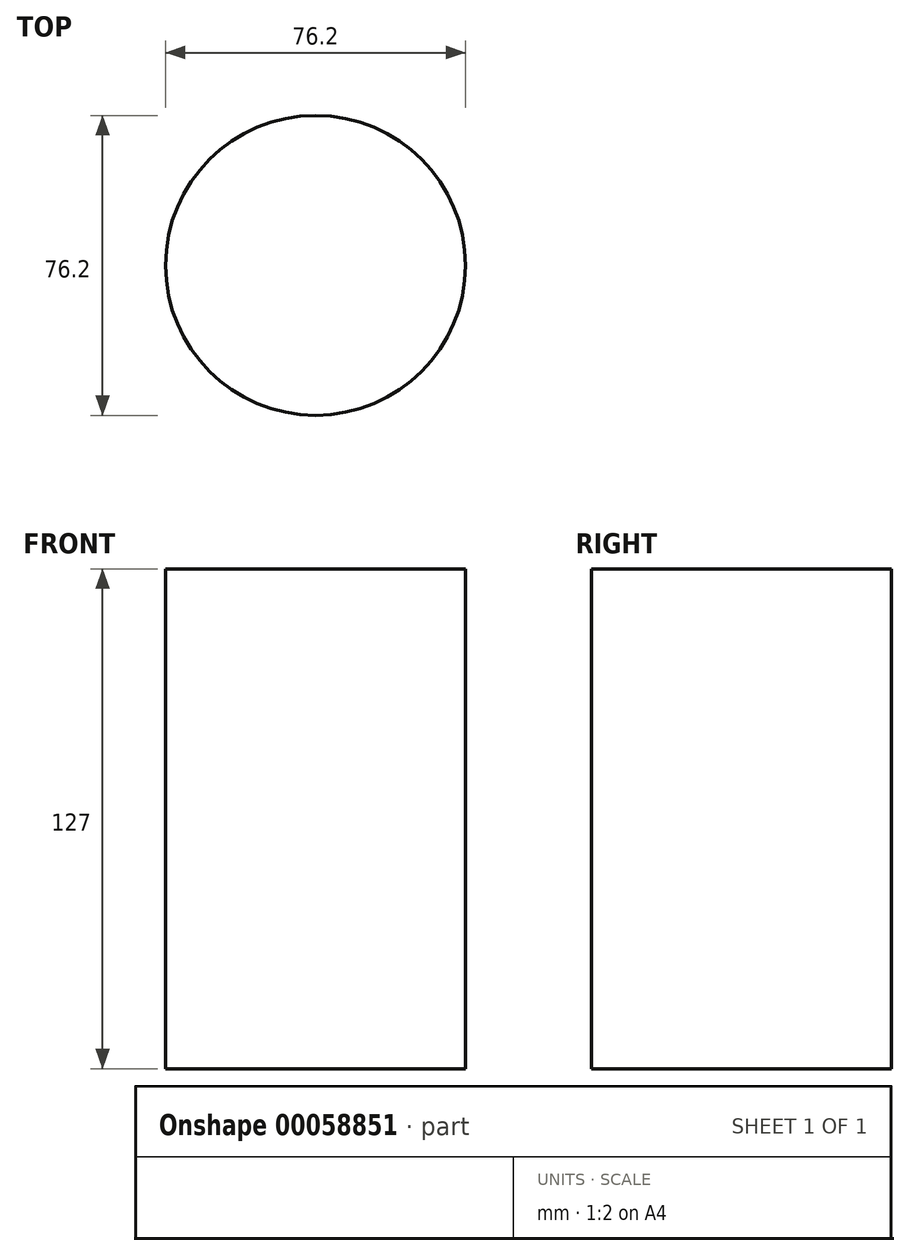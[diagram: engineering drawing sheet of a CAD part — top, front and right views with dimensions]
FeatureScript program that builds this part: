
annotation { "Feature Type Name" : "Feature", "Feature Type Description" : "" }
export const myFeature = defineFeature(function(context is Context, id is Id, definition is map)
    precondition{}
    {
        {
            var Q0;
            Q0=qCreatedBy(makeId("Front.planeOp"),FACE);
            var sketch = newSketch(context, id + "F0", { "sketchPlane" : qUnion([Q0])});
            skLineSegment(sketch, "E0.bottom", {"start": v(-38.1, 63.5) * mm, "end": v(0, 63.5) * mm});
            skLineSegment(sketch, "E0.top", {"start": v(-38.1, -63.5) * mm, "end": v(0, -63.5) * mm});
            skLineSegment(sketch, "E0.left", {"start": v(-38.1, 63.5) * mm, "end": v(-38.1, -63.5) * mm});
            skLineSegment(sketch, "E0.right", {"start": v(0, 63.5) * mm, "end": v(0, -63.5) * mm});
            skSolve(sketch);
        }
        {
            var Q0;
            Q0=makeQuery(id+"F0.imprint","IMPRINT",FACE,{"disambiguationData":[TD([[makeQuery(id+"F0.imprint","IMPRINT",EDGE,{"derivedFrom":sQuery(id+"F0.wireOp",EDGE,"E0.bottom")}),-1.0]])]});
            var Q1;
            Q1=sQuery(id+"F0.wireOp",EDGE,"E0.right");
            revolve(context, id + "F1", {"entities" : qUnion([Q0]), "axis" : qUnion([Q1]), "revolveType" : RevolveType.FULL});
        }
        {
            var Q0;
            Q0=qCreatedBy(makeId("Front.planeOp"),FACE);
            var Q1;
            Q1 = qBodyType(qCreatedBy(id + "F3" ,EDGE), BodyType.WIRE);
            cPlane(context, id + "F2", {"entities" : qUnion([Q0, Q1]), "cplaneType" : CPlaneType.OFFSET, "offset" : 38.1 * mm, "width" : 152.4 * mm, "height" : 152.4 * mm});
        }
        {
            var Q0;
            Q0=qCreatedBy(id+"F2.planeOp",FACE);
            var sketch = newSketch(context, id + "F3", { "sketchPlane" : qUnion([Q0])});
            skCircle(sketch, "E1", {"center": v(0, 0) * mm, "radius": 6.35 * mm});
            skSolve(sketch);
        }
        {
            var Q0;
            Q0=makeQuery(id+"F3.imprint","IMPRINT",FACE,{"disambiguationData":[TD([[makeQuery(id+"F3.imprint","IMPRINT",EDGE,{"derivedFrom":sQuery(id+"F3.wireOp",EDGE,"E1")}),1.0]])]});
            extrude(context, id + "F4", {"entities" : qUnion([Q0]), "depth" : 12.7 * mm});
        }
        {
            var Q0;
            Q0=makeQuery(id+"F4.opExtrude","SWEPT_BODY",BODY,{"disambiguationData":[OSD([sQuery(id+"F3.wireOp",EDGE,"E1")])]});
            var Q1;
            Q1=makeQuery(id+"F1.opRevolve","SWEPT_EDGE",EDGE,{"disambiguationData":[OSD([sQuery(id+"F0.wireOp",EDGE,"E0.bottom"),sQuery(id+"F0.wireOp",EDGE,"E0.left")])]});
            circularPattern(context, id + "F5", {"entities" : qUnion([Q0]), "axis" : qUnion([Q1]), "angle" : 360 * degree, "instanceCount" : round(8), "equalSpace" : true});
        }
        {
            var Q0;
            Q0=makeQuery(id+"F4.opExtrude","SWEPT_BODY",BODY,{"disambiguationData":[OSD([sQuery(id+"F3.wireOp",EDGE,"E1")])]});
            var Q1;
            Q1=makeQuery(id+"F5.opPattern","COPY",BODY,{"derivedFrom":makeQuery(id+"F4.opExtrude","SWEPT_BODY",BODY,{"disambiguationData":[OSD([sQuery(id+"F3.wireOp",EDGE,"E1")])]}),"instanceName":"1"});
            var Q2;
            Q2=makeQuery(id+"F5.opPattern","COPY",BODY,{"derivedFrom":makeQuery(id+"F4.opExtrude","SWEPT_BODY",BODY,{"disambiguationData":[OSD([sQuery(id+"F3.wireOp",EDGE,"E1")])]}),"instanceName":"2"});
            var Q3;
            Q3=makeQuery(id+"F5.opPattern","COPY",BODY,{"derivedFrom":makeQuery(id+"F4.opExtrude","SWEPT_BODY",BODY,{"disambiguationData":[OSD([sQuery(id+"F3.wireOp",EDGE,"E1")])]}),"instanceName":"3"});
            var Q4;
            Q4=makeQuery(id+"F5.opPattern","COPY",BODY,{"derivedFrom":makeQuery(id+"F4.opExtrude","SWEPT_BODY",BODY,{"disambiguationData":[OSD([sQuery(id+"F3.wireOp",EDGE,"E1")])]}),"instanceName":"4"});
            var Q5;
            Q5=makeQuery(id+"F5.opPattern","COPY",BODY,{"derivedFrom":makeQuery(id+"F4.opExtrude","SWEPT_BODY",BODY,{"disambiguationData":[OSD([sQuery(id+"F3.wireOp",EDGE,"E1")])]}),"instanceName":"5"});
            var Q6;
            Q6=makeQuery(id+"F5.opPattern","COPY",BODY,{"derivedFrom":makeQuery(id+"F4.opExtrude","SWEPT_BODY",BODY,{"disambiguationData":[OSD([sQuery(id+"F3.wireOp",EDGE,"E1")])]}),"instanceName":"6"});
            var Q7;
            Q7=makeQuery(id+"F5.opPattern","COPY",BODY,{"derivedFrom":makeQuery(id+"F4.opExtrude","SWEPT_BODY",BODY,{"disambiguationData":[OSD([sQuery(id+"F3.wireOp",EDGE,"E1")])]}),"instanceName":"7"});
            var Q8;
            Q8=makeQuery(id+"F1.opRevolve","SWEPT_BODY",BODY,{"disambiguationData":[OSD([sQuery(id+"F0.wireOp",EDGE,"E0.bottom"),sQuery(id+"F0.wireOp",EDGE,"E0.top"),sQuery(id+"F0.wireOp",EDGE,"E0.left"),sQuery(id+"F0.wireOp",EDGE,"E0.right")])]});
            var Q9;
            Q9=makeQuery(id+"F5.opPattern","COPY",BODY,{"derivedFrom":makeQuery(id+"F1.opRevolve","SWEPT_BODY",BODY,{"disambiguationData":[OSD([sQuery(id+"F0.wireOp",EDGE,"E0.bottom"),sQuery(id+"F0.wireOp",EDGE,"E0.top"),sQuery(id+"F0.wireOp",EDGE,"E0.left"),sQuery(id+"F0.wireOp",EDGE,"E0.right")])]}),"instanceName":"3"});
            var Q10;
            Q10=makeQuery(id+"F5.opPattern","COPY",BODY,{"derivedFrom":makeQuery(id+"F1.opRevolve","SWEPT_BODY",BODY,{"disambiguationData":[OSD([sQuery(id+"F0.wireOp",EDGE,"E0.bottom"),sQuery(id+"F0.wireOp",EDGE,"E0.top"),sQuery(id+"F0.wireOp",EDGE,"E0.left"),sQuery(id+"F0.wireOp",EDGE,"E0.right")])]}),"instanceName":"4"});
            var Q11;
            Q11=makeQuery(id+"F5.opPattern","COPY",BODY,{"derivedFrom":makeQuery(id+"F1.opRevolve","SWEPT_BODY",BODY,{"disambiguationData":[OSD([sQuery(id+"F0.wireOp",EDGE,"E0.bottom"),sQuery(id+"F0.wireOp",EDGE,"E0.top"),sQuery(id+"F0.wireOp",EDGE,"E0.left"),sQuery(id+"F0.wireOp",EDGE,"E0.right")])]}),"instanceName":"5"});
            booleanBodies(context, id + "F6", {"operationType" : BooleanOperationType.SUBTRACTION, "tools" : qUnion([Q0, Q1, Q2, Q3, Q4, Q5, Q6, Q7]), "targets" : qUnion([Q8, Q9, Q10, Q11])});
        }
    });
